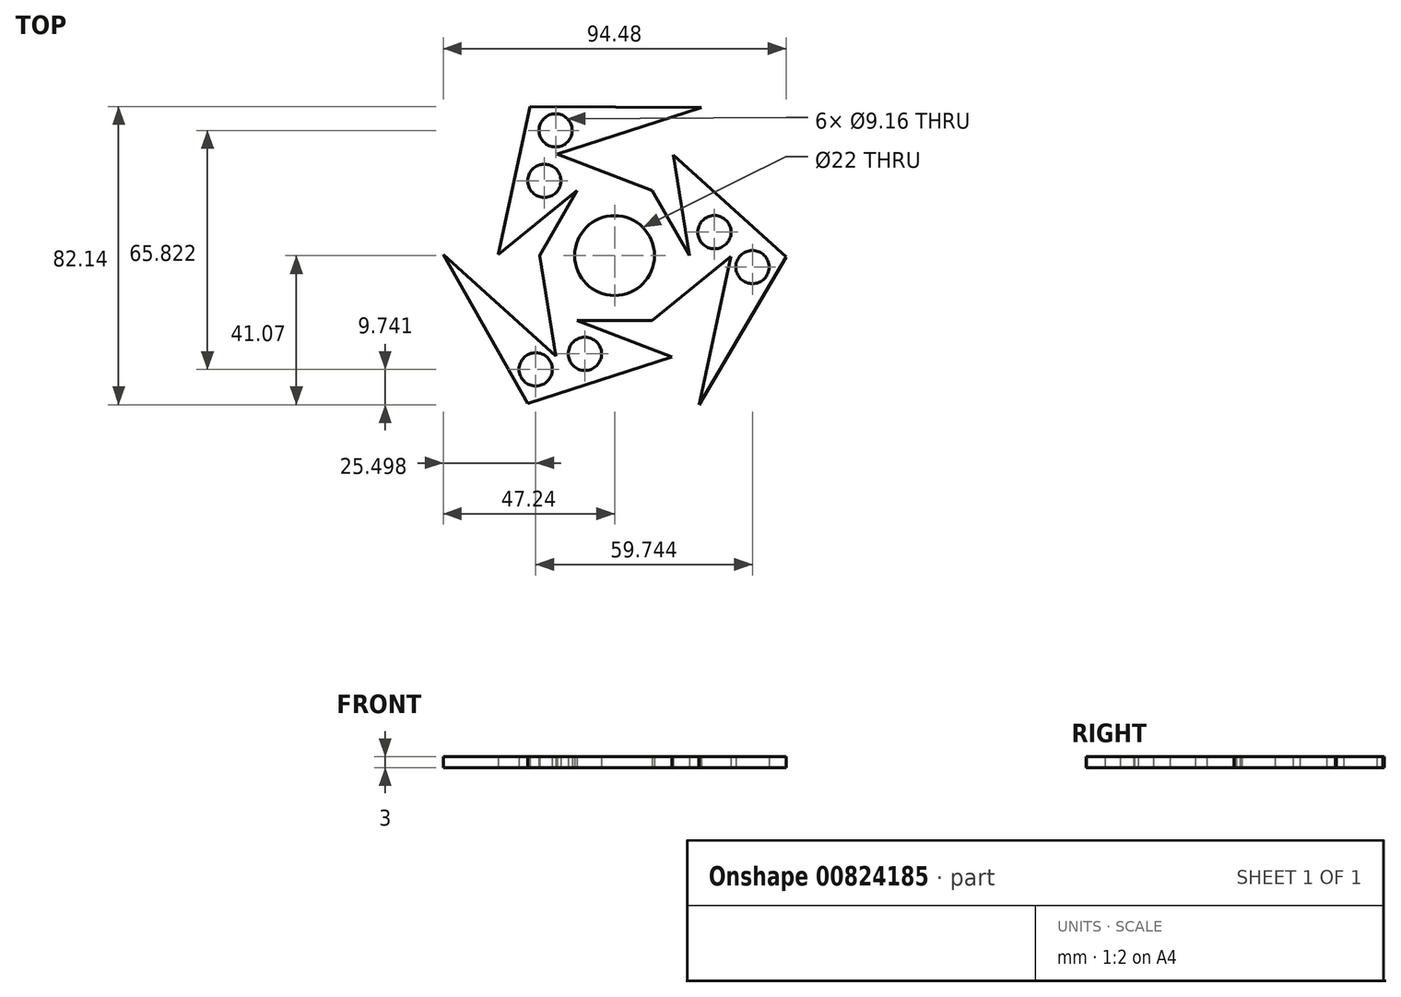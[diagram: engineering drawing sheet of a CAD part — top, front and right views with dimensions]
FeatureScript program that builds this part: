
annotation { "Feature Type Name" : "Feature", "Feature Type Description" : "" }
export const myFeature = defineFeature(function(context is Context, id is Id, definition is map)
    precondition{}
    {
        {
            var Q0;
            Q0=qCreatedBy(makeId("Top.planeOp"),FACE);
            var sketch = newSketch(context, id + "F0", { "sketchPlane" : qUnion([Q0])});
            skLineSegment(sketch, "E0.0", {"start": v(10.34, -17.92) * mm, "end": v(-10.34, -17.92) * mm});
            skPoint(sketch, "E0.0.midPoint", {"position": v(0, -17.92) * mm});
            skPoint(sketch, "E1.0.midPoint", {"position": v(-24.18, -13.74) * mm});
            skLineSegment(sketch, "E2", {"start": v(-20.69, 0) * mm, "end": v(-16.24, -27.7) * mm});
            skLineSegment(sketch, "E3", {"start": v(-10.34, -17.92) * mm, "end": v(15.87, -27.92) * mm});
            skArc(sketch, "E4", {"start": v(-8.4, 0.06) * mm, "mid": v(-8.4, 0.03) * mm, "end": v(-8.4, 0) * mm});
            skPoint(sketch, "E5.0.midPoint", {"position": v(15.87, -27.92) * mm});
            skLineSegment(sketch, "E6.1", {"start": v(-23.9, -40.75) * mm, "end": v(-47.24, 0.32) * mm});
            skPoint(sketch, "E6.0.midPoint", {"position": v(-0.28, -40.91) * mm});
            skLineSegment(sketch, "E7", {"start": v(15.87, -27.92) * mm, "end": v(-23.9, -40.75) * mm});
            skLineSegment(sketch, "E8", {"start": v(-16.24, -27.7) * mm, "end": v(-47.24, 0.32) * mm});
            skCircle(sketch, "E9", {"center": v(-8.17, -27.07) * mm, "radius": 4.58 * mm});
            skCircle(sketch, "E10", {"center": v(-21.74, -31.33) * mm, "radius": 4.58 * mm});
            skLineSegment(sketch, "E11.1.0", {"start": v(10.34, -17.92) * mm, "end": v(32.11, -0.22) * mm});
            skLineSegment(sketch, "E11.1.1", {"start": v(47.24, -0.32) * mm, "end": v(23.34, -41.07) * mm});
            skArc(sketch, "E11.1.2", {"start": v(4.15, -7.3) * mm, "mid": v(4.17, -7.29) * mm, "end": v(4.2, -7.27) * mm});
            skLineSegment(sketch, "E11.1.3", {"start": v(10.34, 17.92) * mm, "end": v(20.69, 0) * mm});
            skPoint(sketch, "E11.1.4", {"position": v(23.99, -14.07) * mm});
            skCircle(sketch, "E11.1.5", {"center": v(27.53, 6.46) * mm, "radius": 4.58 * mm});
            skPoint(sketch, "E11.1.6", {"position": v(16.24, 27.7) * mm});
            skPoint(sketch, "E11.1.7", {"position": v(15.52, 8.96) * mm});
            skCircle(sketch, "E11.1.8", {"center": v(38, -3.16) * mm, "radius": 4.58 * mm});
            skPoint(sketch, "E11.1.9", {"position": v(35.57, 20.22) * mm});
            skLineSegment(sketch, "E11.1.10", {"start": v(16.24, 27.7) * mm, "end": v(47.24, -0.32) * mm});
            skLineSegment(sketch, "E11.1.11", {"start": v(32.11, -0.22) * mm, "end": v(23.34, -41.07) * mm});
            skLineSegment(sketch, "E11.1.12", {"start": v(20.69, 0) * mm, "end": v(16.24, 27.7) * mm});
            skLineSegment(sketch, "E11.2.0", {"start": v(10.34, 17.92) * mm, "end": v(-15.87, 27.92) * mm});
            skLineSegment(sketch, "E11.2.1", {"start": v(-23.34, 41.07) * mm, "end": v(23.9, 40.75) * mm});
            skArc(sketch, "E11.2.2", {"start": v(4.25, 7.24) * mm, "mid": v(4.22, 7.26) * mm, "end": v(4.2, 7.27) * mm});
            skLineSegment(sketch, "E11.2.3", {"start": v(-20.69, 0) * mm, "end": v(-10.34, 17.92) * mm});
            skPoint(sketch, "E11.2.4", {"position": v(0.19, 27.8) * mm});
            skCircle(sketch, "E11.2.5", {"center": v(-19.35, 20.6) * mm, "radius": 4.58 * mm});
            skPoint(sketch, "E11.2.6", {"position": v(-32.11, 0.22) * mm});
            skPoint(sketch, "E11.2.7", {"position": v(-15.52, 8.96) * mm});
            skCircle(sketch, "E11.2.8", {"center": v(-16.26, 34.5) * mm, "radius": 4.58 * mm});
            skPoint(sketch, "E11.2.9", {"position": v(-35.3, 20.7) * mm});
            skLineSegment(sketch, "E11.2.10", {"start": v(-32.11, 0.22) * mm, "end": v(-23.34, 41.07) * mm});
            skLineSegment(sketch, "E11.2.11", {"start": v(-15.87, 27.92) * mm, "end": v(23.9, 40.75) * mm});
            skLineSegment(sketch, "E11.2.12", {"start": v(-10.34, 17.92) * mm, "end": v(-32.11, 0.22) * mm});
            skCircle(sketch, "E12", {"center": v(0, 0) * mm, "radius": 11 * mm});
            skSolve(sketch);
        }
        {
            var Q0;
            Q0=qSketchRegion(id+"F0",true);
            extrude(context, id + "F1", {"entities" : qUnion([Q0]), "depth" : 3 * mm, "offsetDistance" : 25 * mm});
        }
    });
